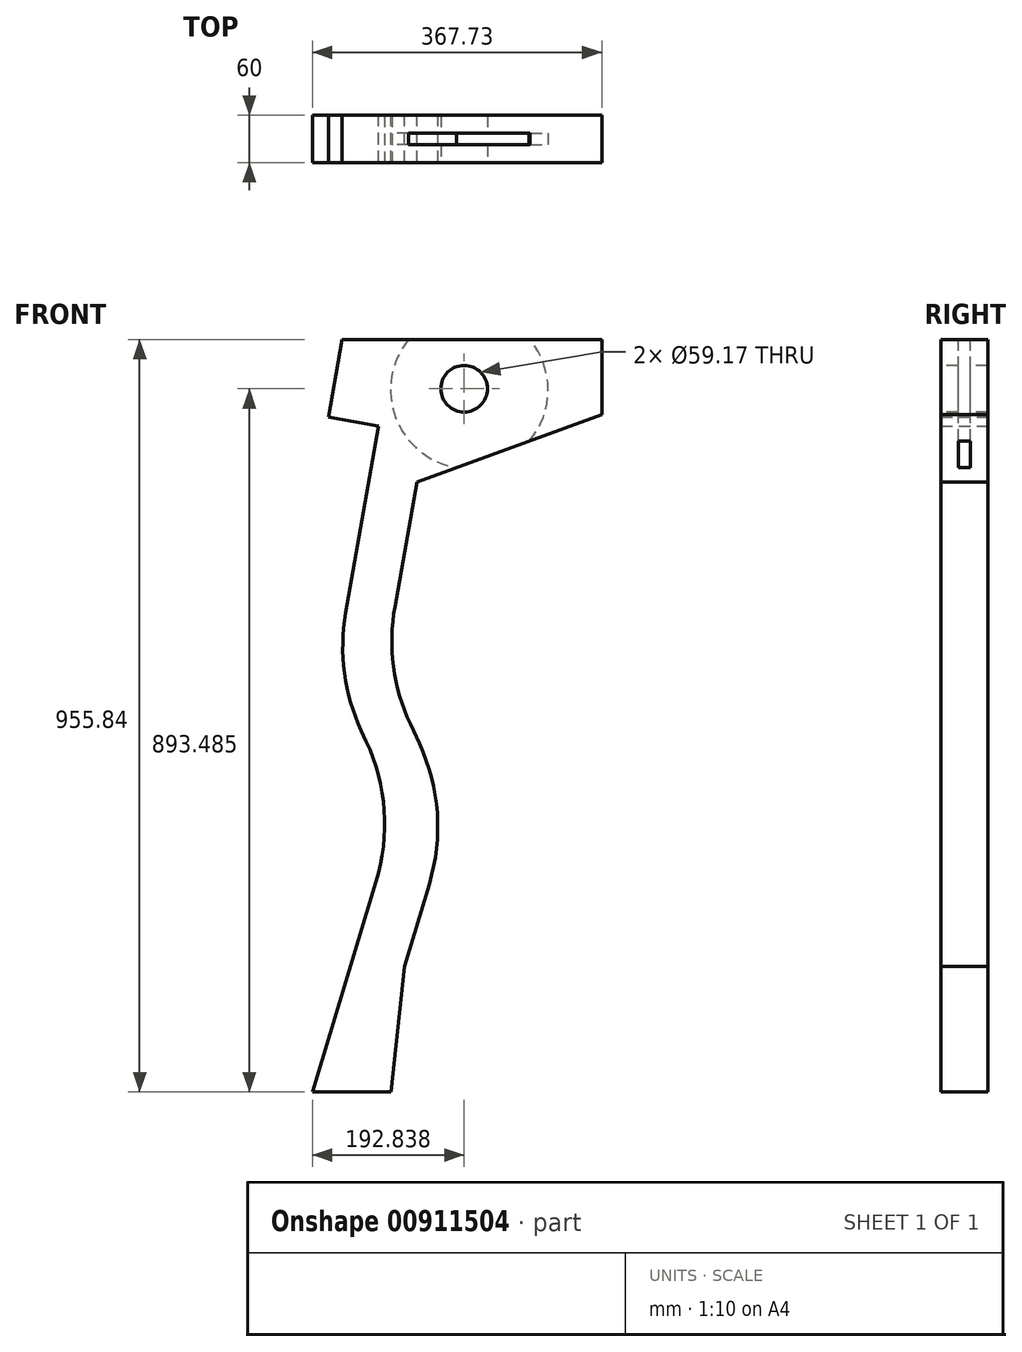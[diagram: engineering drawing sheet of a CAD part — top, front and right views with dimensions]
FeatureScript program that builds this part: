
annotation { "Feature Type Name" : "Feature", "Feature Type Description" : "" }
export const myFeature = defineFeature(function(context is Context, id is Id, definition is map)
    precondition{}
    {
        {
            var Q0;
            Q0=qCreatedBy(makeId("Front.planeOp"),FACE);
            var sketch = newSketch(context, id + "F0", { "sketchPlane" : qUnion([Q0])});
            skLineSegment(sketch, "E0", {"start": v(-15.62, 397.22) * mm, "end": v(-71.24, 81.79) * mm});
            skLineSegment(sketch, "E1", {"start": v(-71.24, 81.79) * mm, "end": v(8.87, -90) * mm});
            skLineSegment(sketch, "E2", {"start": v(8.87, -90) * mm, "end": v(-100, -448.85) * mm});
            skLineSegment(sketch, "E3", {"start": v(16.79, -289.12) * mm, "end": v(76.36, -92.76) * mm});
            skLineSegment(sketch, "E4", {"start": v(76.36, -92.76) * mm, "end": v(-8.87, 90) * mm});
            skLineSegment(sketch, "E5", {"start": v(-8.87, 90) * mm, "end": v(32.8, 326.35) * mm});
            skLineSegment(sketch, "E6", {"start": v(16.79, -289.12) * mm, "end": v(0, -448.85) * mm});
            skLineSegment(sketch, "E7", {"start": v(-100, -448.85) * mm, "end": v(0, -448.85) * mm});
            skLineSegment(sketch, "E8", {"start": v(-15.62, 397.22) * mm, "end": v(-79.63, 408.51) * mm});
            skLineSegment(sketch, "E9", {"start": v(-79.63, 408.51) * mm, "end": v(-62.27, 507) * mm});
            skLineSegment(sketch, "E10", {"start": v(-62.27, 507) * mm, "end": v(267.73, 507) * mm});
            skLineSegment(sketch, "E11", {"start": v(267.73, 507) * mm, "end": v(267.73, 411.86) * mm});
            skLineSegment(sketch, "E12", {"start": v(267.73, 411.86) * mm, "end": v(32.8, 326.35) * mm});
            skLineSegment(sketch, "E13", {"start": v(0, 0) * mm, "end": v(0, 243.14) * mm});
            skSolve(sketch);
        }
        {
            var Q0;
            Q0=makeQuery(id+"F0.imprint","IMPRINT",FACE,{"disambiguationData":[TD([[makeQuery(id+"F0.imprint","IMPRINT",EDGE,{"derivedFrom":sQuery(id+"F0.wireOp",EDGE,"E0")}),1.0]])]});
            extrude(context, id + "F1", {"entities" : qUnion([Q0]), "endBound" : BoundingType.SYMMETRIC, "depth" : 60 * mm, "offsetDistance" : 25 * mm});
        }
        {
            var Q0;
            Q0=makeQuery(id+"F1.opExtrude","SWEPT_EDGE",EDGE,{"disambiguationData":[OSD([sQuery(id+"F0.wireOp",EDGE,"E4"),sQuery(id+"F0.wireOp",EDGE,"E5")])]});
            var Q1;
            Q1=makeQuery(id+"F1.opExtrude","SWEPT_EDGE",EDGE,{"disambiguationData":[OSD([sQuery(id+"F0.wireOp",EDGE,"E3"),sQuery(id+"F0.wireOp",EDGE,"E4")])]});
            var Q2;
            Q2=makeQuery(id+"F1.opExtrude","SWEPT_EDGE",EDGE,{"disambiguationData":[OSD([sQuery(id+"F0.wireOp",EDGE,"E0"),sQuery(id+"F0.wireOp",EDGE,"E1")])]});
            var Q3;
            Q3=makeQuery(id+"F1.opExtrude","SWEPT_EDGE",EDGE,{"disambiguationData":[OSD([sQuery(id+"F0.wireOp",EDGE,"E1"),sQuery(id+"F0.wireOp",EDGE,"E2")])]});
            fillet(context, id + "F2", {"entities" : qUnion([Q0, Q1, Q2, Q3]), "radius" : 250 * mm, "tangentPropagation" : true, "allowEdgeOverflow" : false});
        }
        {
            var Q0;
            Q0=makeQuery(id+"F1.opExtrude","CAP_FACE",FACE,{"disambiguationData":[OSD([sQuery(id+"F0.wireOp",EDGE,"E0"),sQuery(id+"F0.wireOp",EDGE,"E1"),sQuery(id+"F0.wireOp",EDGE,"E2"),sQuery(id+"F0.wireOp",EDGE,"E3"),sQuery(id+"F0.wireOp",EDGE,"E4"),sQuery(id+"F0.wireOp",EDGE,"E5"),sQuery(id+"F0.wireOp",EDGE,"E6"),sQuery(id+"F0.wireOp",EDGE,"E7"),sQuery(id+"F0.wireOp",EDGE,"E8"),sQuery(id+"F0.wireOp",EDGE,"E9"),sQuery(id+"F0.wireOp",EDGE,"E10"),sQuery(id+"F0.wireOp",EDGE,"E11"),sQuery(id+"F0.wireOp",EDGE,"E12")])],"isStart":false});
            var sketch = newSketch(context, id + "F3", { "sketchPlane" : qUnion([Q0])});
            skCircle(sketch, "E14", {"center": v(92.84, 444.63) * mm, "radius": 29.59 * mm});
            skSolve(sketch);
        }
        {
            var Q0;
            Q0=makeQuery(id+"F3.imprint","IMPRINT",FACE,{"disambiguationData":[TD([[makeQuery(id+"F3.imprint","IMPRINT",EDGE,{"derivedFrom":sQuery(id+"F3.wireOp",EDGE,"E14")}),1.0]])]});
            extrude(context, id + "F4", {"entities" : qUnion([Q0]), "operationType" : NewBodyOperationType.REMOVE, "endBound" : BoundingType.THROUGH_ALL, "oppositeDirection" : true, "depth" : 25 * mm, "offsetDistance" : 25 * mm});
        }
        {
            var Q0;
            Q0=qCreatedBy(makeId("Front.planeOp"),FACE);
            var sketch = newSketch(context, id + "F5", { "sketchPlane" : qUnion([Q0])});
            skCircle(sketch, "E15", {"center": v(99.46, 443.24) * mm, "radius": 100 * mm});
            skSolve(sketch);
        }
        {
            var Q0;
            Q0=makeQuery(id+"F5.imprint","IMPRINT",FACE,{"disambiguationData":[TD([[makeQuery(id+"F5.imprint","IMPRINT",EDGE,{"derivedFrom":sQuery(id+"F5.wireOp",EDGE,"E15")}),1.0]])]});
            extrude(context, id + "F6", {"entities" : qUnion([Q0]), "operationType" : NewBodyOperationType.REMOVE, "endBound" : BoundingType.SYMMETRIC, "oppositeDirection" : true, "depth" : 15 * mm, "offsetDistance" : 25 * mm});
        }
    });
